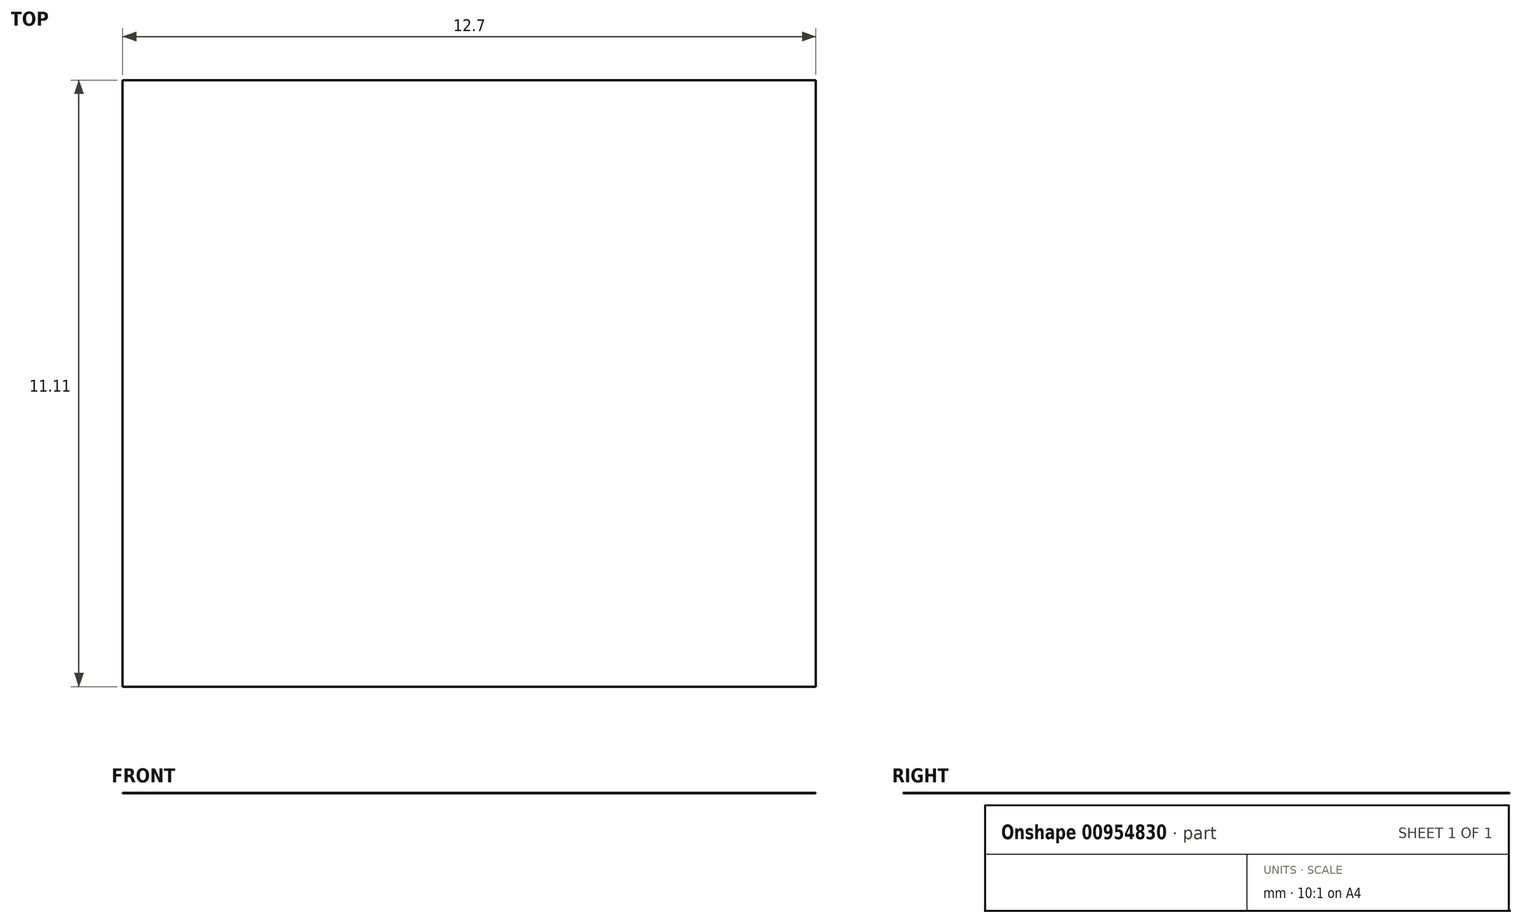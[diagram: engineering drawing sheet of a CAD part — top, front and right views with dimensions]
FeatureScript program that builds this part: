
annotation { "Feature Type Name" : "Feature", "Feature Type Description" : "" }
export const myFeature = defineFeature(function(context is Context, id is Id, definition is map)
    precondition{}
    {
        {
            var Q0;
            Q0=qCreatedBy(makeId("Top.planeOp"),FACE);
            var sketch = newSketch(context, id + "F0", { "sketchPlane" : qUnion([Q0])});
            skLineSegment(sketch, "E0.bottom", {"start": v(0, 0) * mm, "end": v(12.7, 0) * mm});
            skLineSegment(sketch, "E0.top", {"start": v(0, 11.11) * mm, "end": v(12.7, 11.11) * mm});
            skLineSegment(sketch, "E0.left", {"start": v(0, 0) * mm, "end": v(0, 11.11) * mm});
            skLineSegment(sketch, "E0.right", {"start": v(12.7, 0) * mm, "end": v(12.7, 11.11) * mm});
            skSolve(sketch);
        }
        {
            var Q0;
            Q0=makeQuery(id+"F0.imprint","IMPRINT",FACE,{"disambiguationData":[TD([[makeQuery(id+"F0.imprint","IMPRINT",EDGE,{"derivedFrom":sQuery(id+"F0.wireOp",EDGE,"E0.bottom")}),1.0]])]});
            extrude(context, id + "F1", {"entities" : qUnion([Q0]), "depth" : 1 / 101.6 * mm, "offsetDistance" : 25.4 * mm});
        }
        {
            var Q0;
            Q0=makeQuery(id+"F1.opExtrude","SWEPT_FACE",FACE,{"disambiguationData":[OSD([sQuery(id+"F0.wireOp",EDGE,"E0.left")])]});
            var sketch = newSketch(context, id + "F2", { "sketchPlane" : qUnion([Q0])});
            skCircle(sketch, "E1", {"center": v(-10.35, 3.18) * mm, "radius": 0.6 * mm});
            skCircle(sketch, "E2", {"center": v(-8.98, 3.18) * mm, "radius": 0.6 * mm});
            skCircle(sketch, "E3", {"center": v(-7.6, 3.18) * mm, "radius": 0.6 * mm});
            skCircle(sketch, "E4", {"center": v(-6.24, 3.18) * mm, "radius": 0.6 * mm});
            skCircle(sketch, "E5", {"center": v(-4.87, 3.18) * mm, "radius": 0.6 * mm});
            skCircle(sketch, "E6", {"center": v(-3.5, 3.18) * mm, "radius": 0.6 * mm});
            skCircle(sketch, "E7", {"center": v(-2.13, 3.18) * mm, "radius": 0.6 * mm});
            skCircle(sketch, "E8", {"center": v(-0.76, 3.18) * mm, "radius": 0.6 * mm});
            skSolve(sketch);
        }
        {
            var Q0;
            Q0 = qSketchRegion(id + "F2", true);
            extrude(context, id + "F3", {"entities" : qUnion([Q0]), "operationType" : NewBodyOperationType.REMOVE, "endBound" : BoundingType.THROUGH_ALL, "oppositeDirection" : true, "depth" : 25.4 * mm, "offsetDistance" : 25.4 * mm});
        }
        {
            var Q0;
            Q0=makeQuery(id+"F1.opExtrude","CAP_FACE",FACE,{"disambiguationData":[OSD([sQuery(id+"F0.wireOp",EDGE,"E0.bottom"),sQuery(id+"F0.wireOp",EDGE,"E0.top"),sQuery(id+"F0.wireOp",EDGE,"E0.left"),sQuery(id+"F0.wireOp",EDGE,"E0.right")])],"isStart":false});
            extrude(context, id + "F4", {"entities" : qUnion([Q0]), "operationType" : NewBodyOperationType.REMOVE, "oppositeDirection" : true, "depth" : 1 / 203.2 * mm, "offsetDistance" : 25.4 * mm});
        }
    });
